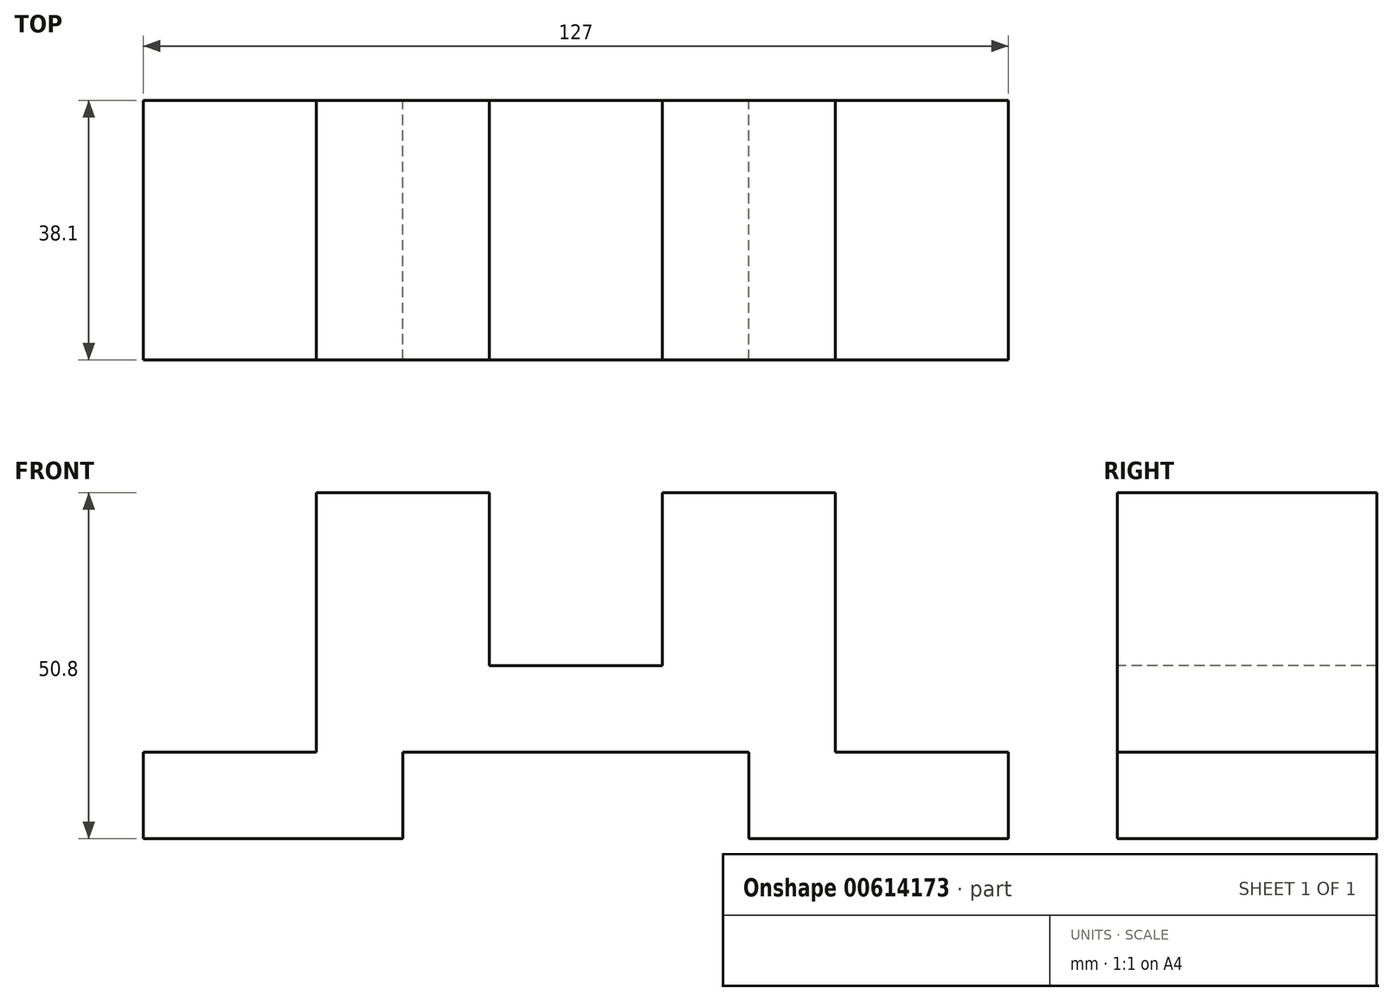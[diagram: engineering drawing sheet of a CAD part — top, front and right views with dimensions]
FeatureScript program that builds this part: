
annotation { "Feature Type Name" : "Feature", "Feature Type Description" : "" }
export const myFeature = defineFeature(function(context is Context, id is Id, definition is map)
    precondition{}
    {
        {
            var Q0;
            Q0=qCreatedBy(makeId("Front.planeOp"),FACE);
            var sketch = newSketch(context, id + "F0", { "sketchPlane" : qUnion([Q0])});
            skLineSegment(sketch, "E0.bottom", {"start": v(63.5, 25.4) * mm, "end": v(-63.5, 25.4) * mm});
            skLineSegment(sketch, "E0.top", {"start": v(63.5, -25.4) * mm, "end": v(-63.5, -25.4) * mm});
            skLineSegment(sketch, "E0.left", {"start": v(63.5, 25.4) * mm, "end": v(63.5, -25.4) * mm});
            skLineSegment(sketch, "E0.right", {"start": v(-63.5, 25.4) * mm, "end": v(-63.5, -25.4) * mm});
            skPoint(sketch, "E0.middle", {"position": v(0, 0) * mm});
            skSolve(sketch);
        }
        {
            var Q0;
            Q0=makeQuery(id+"F0.imprint","IMPRINT",FACE,{"disambiguationData":[TD([[makeQuery(id+"F0.imprint","IMPRINT",EDGE,{"derivedFrom":sQuery(id+"F0.wireOp",EDGE,"E0.bottom")}),1.0]])]});
            extrude(context, id + "F1", {"entities" : qUnion([Q0]), "depth" : 38.1 * mm, "offsetDistance" : 25.4 * mm});
        }
        {
            var Q0;
            Q0=makeQuery(id+"F1.opExtrude","SWEPT_FACE",FACE,{"disambiguationData":[OSD([sQuery(id+"F0.wireOp",EDGE,"E0.top")])]});
            var sketch = newSketch(context, id + "F2", { "sketchPlane" : qUnion([Q0])});
            skLineSegment(sketch, "E1.bottom", {"start": v(-25.4, 38.1) * mm, "end": v(25.4, 38.1) * mm});
            skLineSegment(sketch, "E1.top", {"start": v(-25.4, 0) * mm, "end": v(25.4, 0) * mm});
            skLineSegment(sketch, "E1.left", {"start": v(-25.4, 38.1) * mm, "end": v(-25.4, 0) * mm});
            skLineSegment(sketch, "E1.right", {"start": v(25.4, 38.1) * mm, "end": v(25.4, 0) * mm});
            skSolve(sketch);
        }
        {
            var Q0;
            Q0 = qSketchRegion(id + "F2", true);
            extrude(context, id + "F3", {"entities" : qUnion([Q0]), "operationType" : NewBodyOperationType.REMOVE, "oppositeDirection" : true, "depth" : 12.7 * mm, "offsetDistance" : 25.4 * mm});
        }
        {
            var Q0;
            Q0=makeQuery(id+"F1.opExtrude","CAP_FACE",FACE,{"disambiguationData":[OSD([sQuery(id+"F0.wireOp",EDGE,"E0.bottom"),sQuery(id+"F0.wireOp",EDGE,"E0.top"),sQuery(id+"F0.wireOp",EDGE,"E0.left"),sQuery(id+"F0.wireOp",EDGE,"E0.right")])],"isStart":false});
            var sketch = newSketch(context, id + "F4", { "sketchPlane" : qUnion([Q0])});
            skLineSegment(sketch, "E2.bottom", {"start": v(-63.5, 25.4) * mm, "end": v(-38.1, 25.4) * mm});
            skLineSegment(sketch, "E2.top", {"start": v(-63.5, -12.7) * mm, "end": v(-38.1, -12.7) * mm});
            skLineSegment(sketch, "E2.left", {"start": v(-63.5, 25.4) * mm, "end": v(-63.5, -12.7) * mm});
            skLineSegment(sketch, "E2.right", {"start": v(-38.1, 25.4) * mm, "end": v(-38.1, -12.7) * mm});
            skSolve(sketch);
        }
        {
            var Q0;
            Q0 = qSketchRegion(id + "F4", true);
            extrude(context, id + "F5", {"entities" : qUnion([Q0]), "operationType" : NewBodyOperationType.REMOVE, "oppositeDirection" : true, "depth" : 38.1 * mm, "offsetDistance" : 25.4 * mm});
        }
        {
            var Q0;
            Q0=makeQuery(id+"F1.opExtrude","CAP_FACE",FACE,{"disambiguationData":[OSD([sQuery(id+"F0.wireOp",EDGE,"E0.bottom"),sQuery(id+"F0.wireOp",EDGE,"E0.top"),sQuery(id+"F0.wireOp",EDGE,"E0.left"),sQuery(id+"F0.wireOp",EDGE,"E0.right")])],"isStart":false});
            var sketch = newSketch(context, id + "F6", { "sketchPlane" : qUnion([Q0])});
            skLineSegment(sketch, "E3.bottom", {"start": v(63.5, 25.4) * mm, "end": v(38.1, 25.4) * mm});
            skLineSegment(sketch, "E3.top", {"start": v(63.5, -12.7) * mm, "end": v(38.1, -12.7) * mm});
            skLineSegment(sketch, "E3.left", {"start": v(63.5, 25.4) * mm, "end": v(63.5, -12.7) * mm});
            skLineSegment(sketch, "E3.right", {"start": v(38.1, 25.4) * mm, "end": v(38.1, -12.7) * mm});
            skSolve(sketch);
        }
        {
            var Q0;
            Q0 = qSketchRegion(id + "F6", true);
            extrude(context, id + "F7", {"entities" : qUnion([Q0]), "operationType" : NewBodyOperationType.REMOVE, "oppositeDirection" : true, "depth" : 38.1 * mm, "offsetDistance" : 25.4 * mm});
        }
        {
            var Q0;
            Q0=makeQuery(id+"F1.opExtrude","SWEPT_FACE",FACE,{"disambiguationData":[OSD([sQuery(id+"F0.wireOp",EDGE,"E0.bottom")])]});
            var sketch = newSketch(context, id + "F8", { "sketchPlane" : qUnion([Q0])});
            skLineSegment(sketch, "E4.bottom", {"start": v(-12.7, 0) * mm, "end": v(12.7, 0) * mm});
            skLineSegment(sketch, "E4.top", {"start": v(-12.7, -38.1) * mm, "end": v(12.7, -38.1) * mm});
            skLineSegment(sketch, "E4.left", {"start": v(-12.7, 0) * mm, "end": v(-12.7, -38.1) * mm});
            skLineSegment(sketch, "E4.right", {"start": v(12.7, 0) * mm, "end": v(12.7, -38.1) * mm});
            skSolve(sketch);
        }
        {
            var Q0;
            Q0 = qSketchRegion(id + "F8", true);
            extrude(context, id + "F9", {"entities" : qUnion([Q0]), "operationType" : NewBodyOperationType.REMOVE, "oppositeDirection" : true, "depth" : 25.4 * mm, "offsetDistance" : 25.4 * mm});
        }
    });
